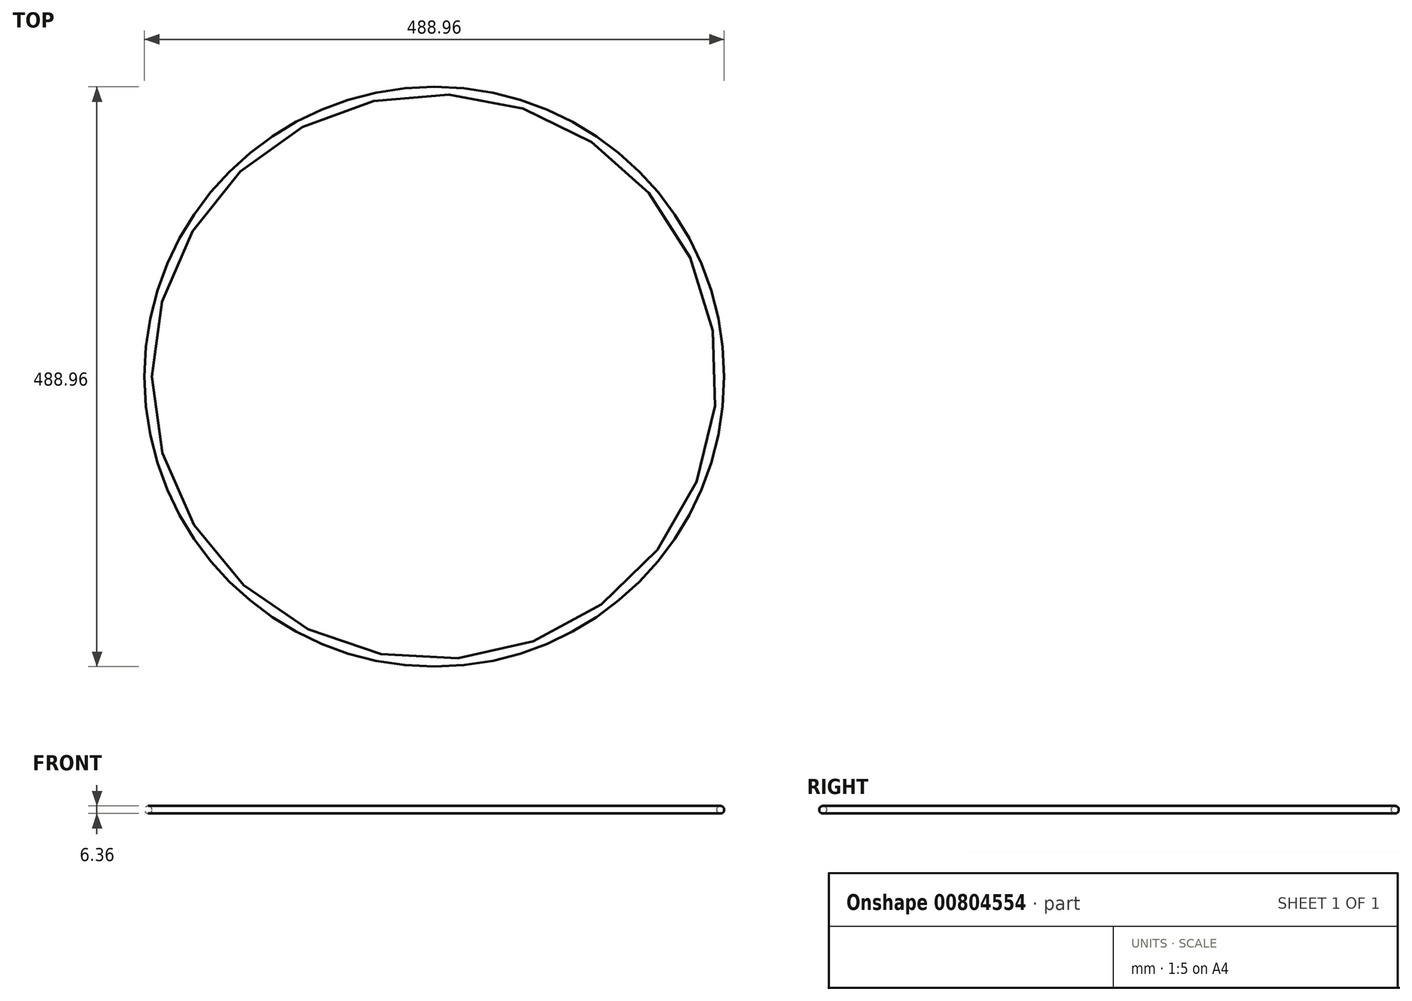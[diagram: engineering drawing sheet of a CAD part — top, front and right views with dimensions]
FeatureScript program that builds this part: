
annotation { "Feature Type Name" : "Feature", "Feature Type Description" : "" }
export const myFeature = defineFeature(function(context is Context, id is Id, definition is map)
    precondition{}
    {
        {
            var Q0;
            Q0=qCreatedBy(makeId("Front.planeOp"),FACE);
            var sketch = newSketch(context, id + "F0", { "sketchPlane" : qUnion([Q0])});
            skCircle(sketch, "E0", {"center": v(241.3, 0) * mm, "radius": 3.18 * mm});
            skLineSegment(sketch, "E1", {"start": v(0, 0) * mm, "end": v(0, 32.12) * mm, "construction": true});
            skSolve(sketch);
        }
        {
            var Q0;
            Q0=makeQuery(id+"F0.imprint","IMPRINT",FACE,{"disambiguationData":[TD([[makeQuery(id+"F0.imprint","IMPRINT",EDGE,{"derivedFrom":sQuery(id+"F0.wireOp",EDGE,"E0")}),1.0]])]});
            var Q1;
            Q1=sQuery(id+"F0.wireOp",EDGE,"E1");
            revolve(context, id + "F1", {"surfaceOperationType" : NewSurfaceOperationType.NEW, "entities" : qUnion([Q0]), "axis" : qUnion([Q1]), "revolveType" : RevolveType.FULL});
        }
    });
